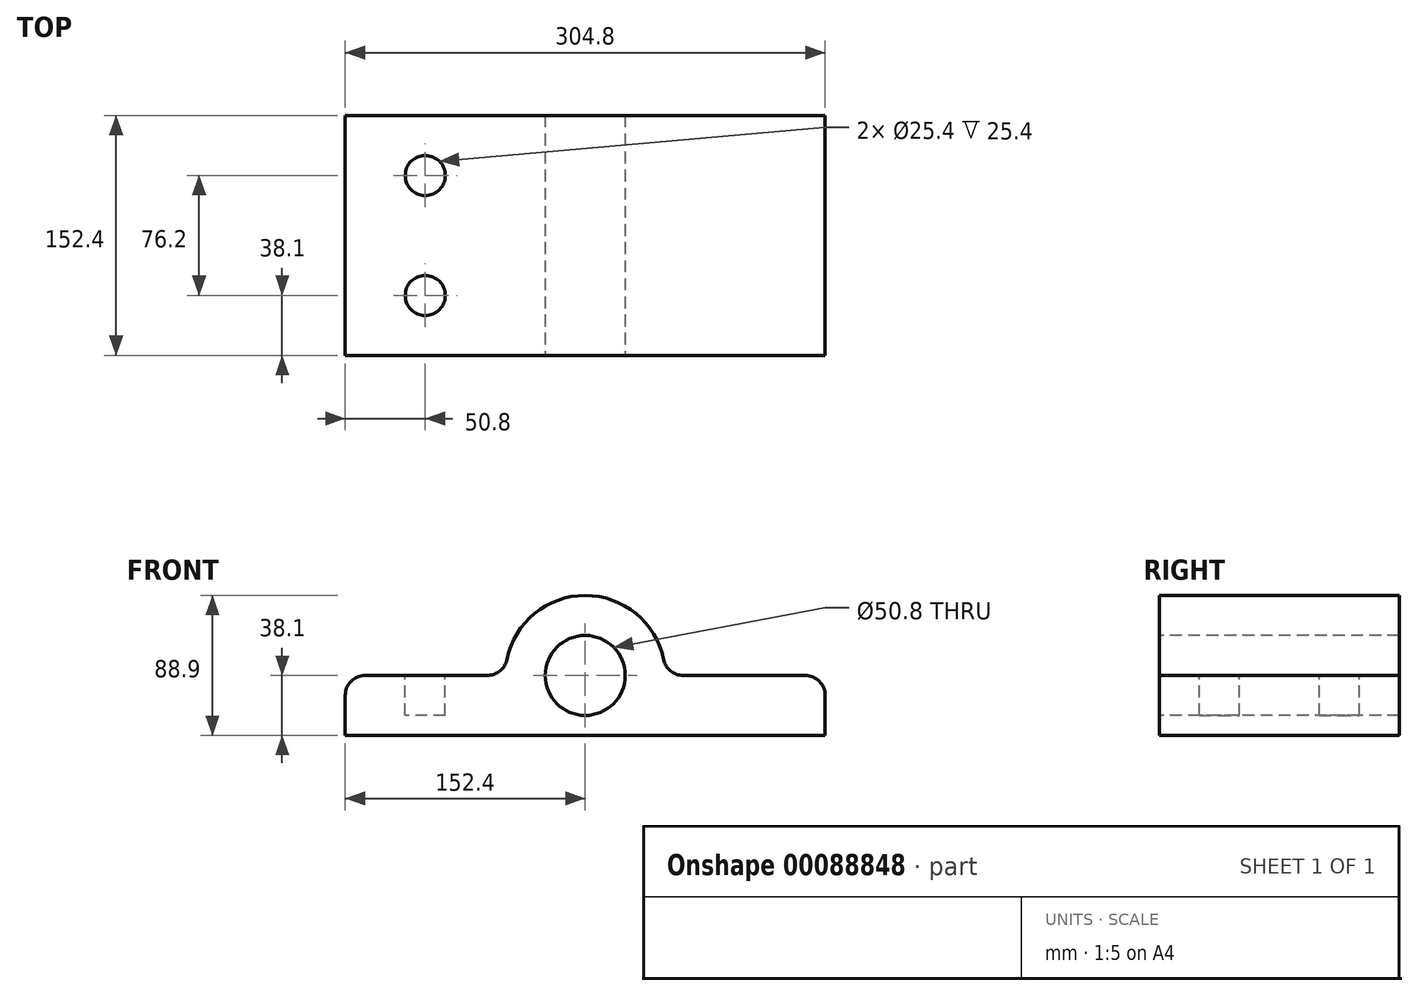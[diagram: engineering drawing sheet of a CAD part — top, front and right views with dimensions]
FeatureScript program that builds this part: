
annotation { "Feature Type Name" : "Feature", "Feature Type Description" : "" }
export const myFeature = defineFeature(function(context is Context, id is Id, definition is map)
    precondition{}
    {
        {
            var Q0;
            Q0=qCreatedBy(makeId("Front.planeOp"),FACE);
            var sketch = newSketch(context, id + "F0", { "sketchPlane" : qUnion([Q0])});
            skLineSegment(sketch, "E0", {"start": v(-152.4, 0) * mm, "end": v(152.4, 0) * mm});
            skLineSegment(sketch, "E1", {"start": v(-152.4, 0) * mm, "end": v(-152.4, 25.4) * mm});
            skLineSegment(sketch, "E2", {"start": v(-139.7, 38.1) * mm, "end": v(-62.22, 38.1) * mm});
            skLineSegment(sketch, "E3", {"start": v(152.4, 0) * mm, "end": v(152.4, 25.4) * mm});
            skLineSegment(sketch, "E4", {"start": v(139.7, 38.1) * mm, "end": v(62.22, 38.1) * mm});
            skArc(sketch, "E5", {"start": v(49.77, 48.26) * mm, "mid": v(0, 88.9) * mm, "end": v(-49.77, 48.26) * mm});
            skCircle(sketch, "E6", {"center": v(0, 38.1) * mm, "radius": 25.4 * mm});
            skPoint(sketch, "E7.visualSharp", {"position": v(-50.8, 38.1) * mm});
            skArc(sketch, "E7.filletArc", {"start": v(-62.22, 38.1) * mm, "mid": v(-54.18, 40.96) * mm, "end": v(-49.77, 48.26) * mm});
            skPoint(sketch, "E8.visualSharp", {"position": v(50.8, 38.1) * mm});
            skArc(sketch, "E8.filletArc", {"start": v(49.77, 48.26) * mm, "mid": v(54.18, 40.96) * mm, "end": v(62.22, 38.1) * mm});
            skPoint(sketch, "E9.visualSharp", {"position": v(-152.4, 38.1) * mm});
            skArc(sketch, "E9.filletArc", {"start": v(-139.7, 38.1) * mm, "mid": v(-148.68, 34.38) * mm, "end": v(-152.4, 25.4) * mm});
            skPoint(sketch, "E10.visualSharp", {"position": v(152.4, 38.1) * mm});
            skArc(sketch, "E10.filletArc", {"start": v(152.4, 25.4) * mm, "mid": v(148.68, 34.38) * mm, "end": v(139.7, 38.1) * mm});
            skSolve(sketch);
        }
        {
            var Q0;
            Q0 = qSketchRegion(id + "F0", true);
            extrude(context, id + "F1", {"entities" : qUnion([Q0]), "oppositeDirection" : true, "depth" : 152.4 * mm});
        }
        {
            var Q0;
            Q0=makeQuery(id+"F1.opExtrude","SWEPT_FACE",FACE,{"disambiguationData":[OSD([sQuery(id+"F0.wireOp",EDGE,"E2")])]});
            var sketch = newSketch(context, id + "F2", { "sketchPlane" : qUnion([Q0])});
            skCircle(sketch, "E11", {"center": v(-101.6, 114.3) * mm, "radius": 12.7 * mm});
            skCircle(sketch, "E12", {"center": v(-101.6, 38.1) * mm, "radius": 12.7 * mm});
            skLineSegment(sketch, "E13", {"start": v(-101.6, 152.4) * mm, "end": v(-101.6, 0) * mm, "construction": true});
            skCircle(sketch, "E14.MirrorC", {"center": v(101.6, 114.3) * mm, "radius": 12.7 * mm});
            skCircle(sketch, "E15.MirrorC", {"center": v(101.6, 38.1) * mm, "radius": 12.7 * mm});
            skSolve(sketch);
        }
        {
            var Q0;
            Q0=makeQuery(id+"F2.imprint","IMPRINT",FACE,{"disambiguationData":[TD([[makeQuery(id+"F2.imprint","IMPRINT",EDGE,{"derivedFrom":sQuery(id+"F2.wireOp",EDGE,"E11")}),1.0]])]});
            var Q1;
            Q1=makeQuery(id+"F2.imprint","IMPRINT",FACE,{"disambiguationData":[TD([[makeQuery(id+"F2.imprint","IMPRINT",EDGE,{"derivedFrom":sQuery(id+"F2.wireOp",EDGE,"E12")}),1.0]])]});
            var Q2;
            Q2=makeQuery(id+"F2.imprint","IMPRINT",FACE,{"disambiguationData":[TD([[makeQuery(id+"F2.imprint","IMPRINT",EDGE,{"derivedFrom":sQuery(id+"F2.wireOp",EDGE,"E14.MirrorC")}),-1.0]])]});
            var Q3;
            Q3=makeQuery(id+"F2.imprint","IMPRINT",FACE,{"disambiguationData":[TD([[makeQuery(id+"F2.imprint","IMPRINT",EDGE,{"derivedFrom":sQuery(id+"F2.wireOp",EDGE,"E15.MirrorC")}),-1.0]])]});
            extrude(context, id + "F3", {"entities" : qUnion([Q0, Q1, Q2, Q3]), "operationType" : NewBodyOperationType.REMOVE, "oppositeDirection" : true, "depth" : 25.4 * mm});
        }
    });
